# Revit family: York CB-PBE-YK - Linear Passive Diffuser, Chilled Beam, Face Hosted, Revit 2015 R1.0
name_source: partatom
category: Mechanical Equipment
revit_build: Autodesk Revit 2015 (Build: 20160512_1515(x64)
units: mm (PartAtom-declared; Revit-internal decimal feet)

## types (1)
- CB-PBE-YK
    (0) Front and Back Supply = Yes
    (1) Front Supply = No
    (2) Back Supply = No
    10 Feet = Yes
    10 Inches = No
    12 Inches = Yes
    13 Inches = No
    17 Inches = No
    18 Inches = No
    2 Feet = No
    22 Inches = No
    24 Inches = Yes
    3 Feet = No
    4 Feet = No
    5 Feet = No
    6 Feet = No
    7 Feet = No
    8 Feet = No
    8 Inches = No
    9 Feet = No
    Adjustable Mounting Brackets = Yes
    Blade Length = 119 1/4"
    Blade Offset = 1/2"
    Chilled Water Connection Diameter = 0"
    Circular Perforation = No
    Clearance = 4"
    Clearance Material = Clearance
    Coil Diameter = 1/2"
    Coil Front Offset = 1"
    Coil Height = 2 1/4"
    Coil Side Offset = 8 5/16"
    Coil Side Offset 1 = 7 1/16"
    Coil Void Diameter = 7/16"
    Default Elevation = 48"
    Description = Exposed Passive Chilled Beam
    Distance Between Support = 40"
    H12 - SS Flex Hose - 12in = No
    H18 - SS Flex Hose - 18in = No
    H24 - SS Flex Hose - 24in = No
    Heating Water Connection Diameter = 0"
    Height = 12"
    Length = 119 3/4"
    Linear Bar Grille = Yes
    MPT  Male Pipe Thread = No
    Manufacturer = York
    Material = Casing:  G90 20GA Galvanealed sheet metal
    Model = CB-PBE-YK
    Neck Size = 0"
    Neck Velocity = 0 FPM
    Nominal Length = 120"
    Nominal Width = 24"
    Number of Bars = 48
    Perforated Base = Parforated Face
    Perforated Circle Radius = 1/16"
    Pipe Material = Copper Pipe
    Plenum Thickness = 1/4"
    SWT  Sweat = Yes
    Select a Beam Height = 3
    Select a Beam Length = 10
    Select a Beam Width = 5
    Select a Water-Coil Piping Connection Type = 1
    URL = http://www.york.com
    Version = 3
    Water Connection Location Selection = 0
    Width = 23 3/4"

## geometry (parser evidence)
native form markers: Blend x2, Sweep x10
no freeform markers — native parametric forms only
